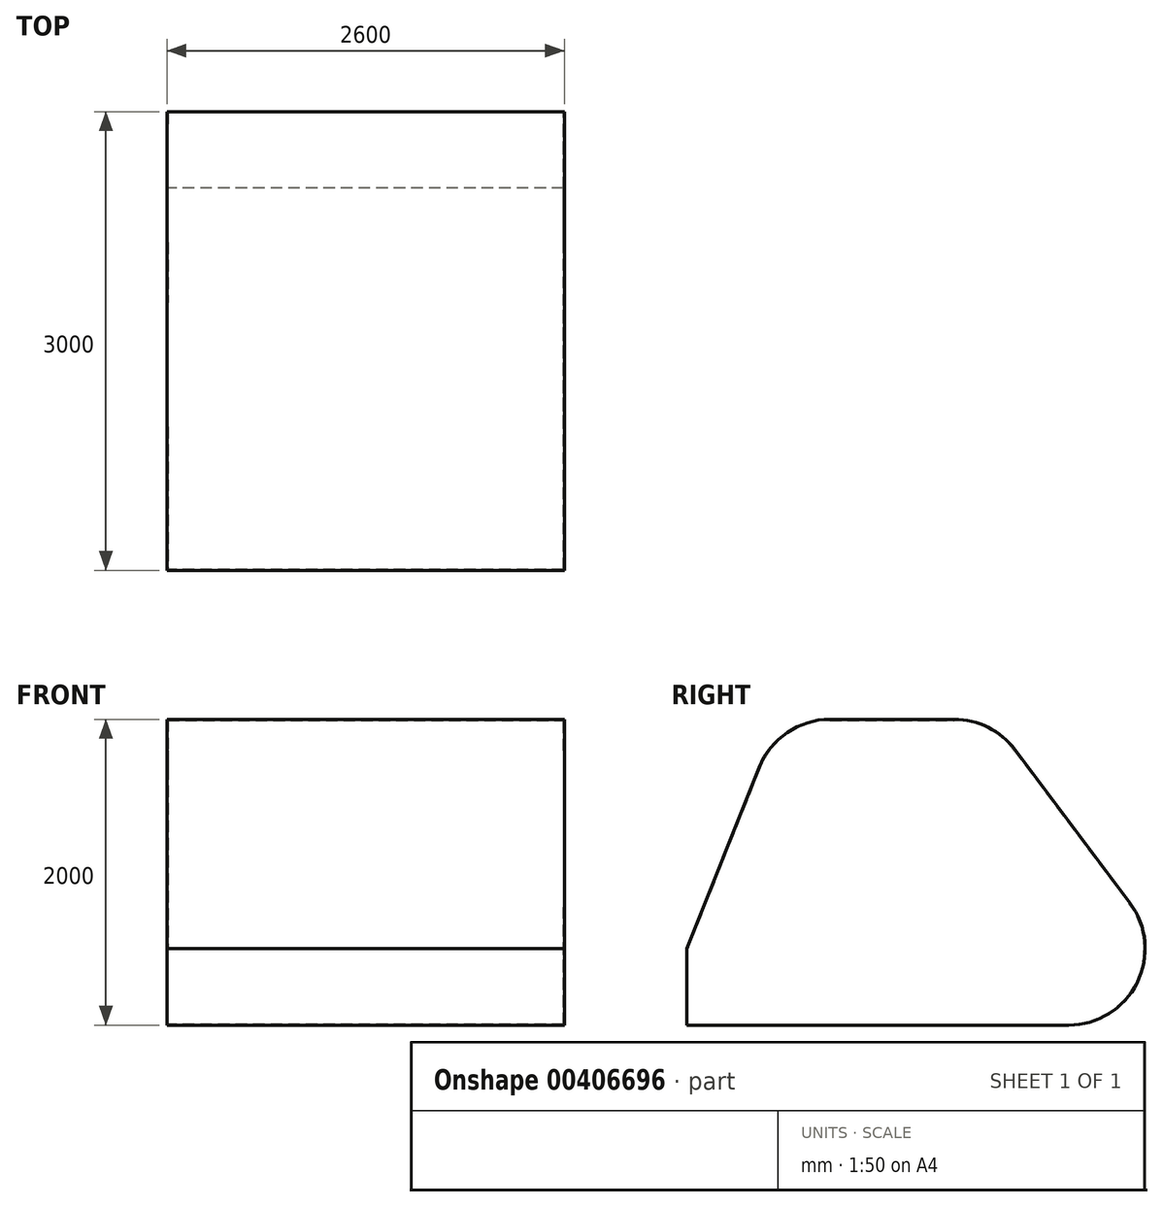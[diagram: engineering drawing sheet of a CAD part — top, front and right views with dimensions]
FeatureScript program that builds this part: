
annotation { "Feature Type Name" : "Feature", "Feature Type Description" : "" }
export const myFeature = defineFeature(function(context is Context, id is Id, definition is map)
    precondition{}
    {
        {
            var Q0;
            Q0=qCreatedBy(makeId("Right.planeOp"),FACE);
            var sketch = newSketch(context, id + "F0", { "sketchPlane" : qUnion([Q0])});
            skLineSegment(sketch, "E0.bottom", {"start": v(0, 0) * mm, "end": v(2500, 0) * mm});
            skLineSegment(sketch, "E0.top", {"start": v(600, 2000) * mm, "end": v(2000, 2000) * mm});
            skLineSegment(sketch, "E0.left", {"start": v(0, 0) * mm, "end": v(0, 500) * mm});
            skLineSegment(sketch, "E1", {"start": v(600, 2000) * mm, "end": v(0, 500) * mm});
            skLineSegment(sketch, "E2", {"start": v(0, 500) * mm, "end": v(3578.17, 500) * mm, "construction": true});
            skLineSegment(sketch, "E3", {"start": v(2500, 2614.96) * mm, "end": v(2500, -587.17) * mm, "construction": true});
            skArc(sketch, "E4", {"start": v(2500, 0) * mm, "mid": v(2947.21, 276.4) * mm, "end": v(2900, 800) * mm});
            skLineSegment(sketch, "E5", {"start": v(2000, 2614.96) * mm, "end": v(2000, -587.17) * mm, "construction": true});
            skLineSegment(sketch, "E6", {"start": v(2000, 2000) * mm, "end": v(2900, 800) * mm});
            skPoint(sketch, "E7.orphan", {"position": v(3000, 2000) * mm});
            skSolve(sketch);
        }
        {
            var Q0;
            Q0=makeQuery(id+"F0.imprint","IMPRINT",FACE,{"disambiguationData":[TD([[makeQuery(id+"F0.imprint","IMPRINT",EDGE,{"derivedFrom":sQuery(id+"F0.wireOp",EDGE,"E0.bottom")}),1.0]])]});
            extrude(context, id + "F1", {"entities" : qUnion([Q0]), "endBound" : BoundingType.SYMMETRIC, "depth" : 2600 * mm});
        }
        {
            var Q0;
            Q0=makeQuery(id+"F1.opExtrude","SWEPT_EDGE",EDGE,{"disambiguationData":[OSD([sQuery(id+"F0.wireOp",EDGE,"E0.top"),sQuery(id+"F0.wireOp",EDGE,"E1")])]});
            var Q1;
            Q1=makeQuery(id+"F1.opExtrude","SWEPT_EDGE",EDGE,{"disambiguationData":[OSD([sQuery(id+"F0.wireOp",EDGE,"E0.top"),sQuery(id+"F0.wireOp",EDGE,"E6")])]});
            fillet(context, id + "F2", {"entities" : qUnion([Q0, Q1]), "radius" : 500 * mm, "tangentPropagation" : true, "allowEdgeOverflow" : false});
        }
        {
            var Q0;
            Q0=makeQuery(id+"F1.opExtrude","SWEPT_FACE",FACE,{"disambiguationData":[OSD([sQuery(id+"F0.wireOp",EDGE,"E0.bottom")])]});
            shell(context, id + "F3", {"entities" : qUnion([Q0]), "thickness" : 6 * mm});
        }
    });
